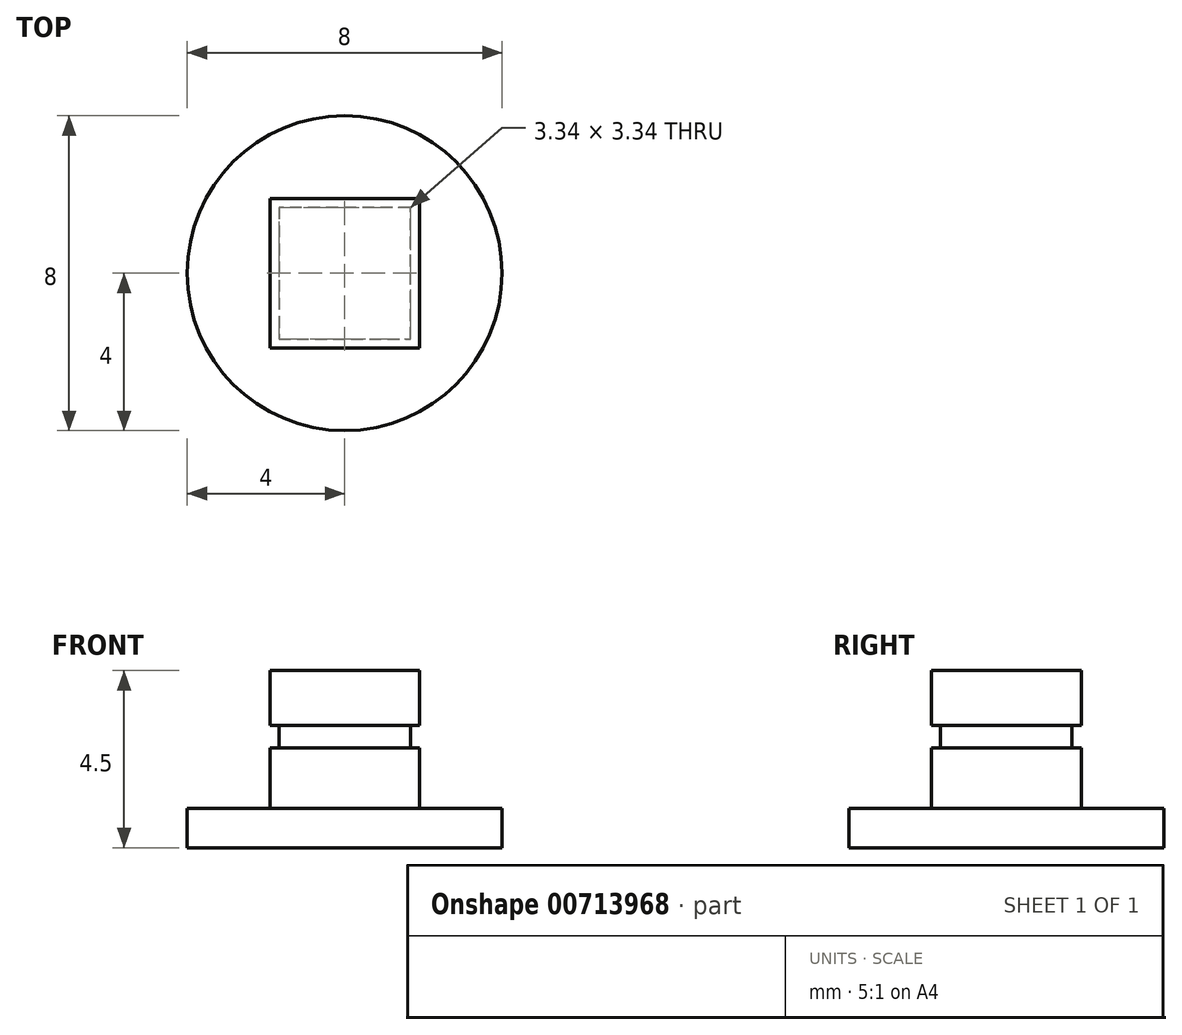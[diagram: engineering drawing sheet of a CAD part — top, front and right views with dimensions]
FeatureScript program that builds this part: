
annotation { "Feature Type Name" : "Feature", "Feature Type Description" : "" }
export const myFeature = defineFeature(function(context is Context, id is Id, definition is map)
    precondition{}
    {
        {
            var Q0;
            Q0=qCreatedBy(makeId("Top.planeOp"),FACE);
            var sketch = newSketch(context, id + "F0", { "sketchPlane" : qUnion([Q0])});
            skCircle(sketch, "E0", {"center": v(0, 0) * mm, "radius": 4 * mm});
            skSolve(sketch);
        }
        {
            var Q0;
            Q0 = qSketchRegion(id + "F0", true);
            extrude(context, id + "F1", {"entities" : qUnion([Q0]), "depth" : 1 * mm, "offsetDistance" : 25 * mm});
        }
        {
            var Q0;
            Q0=makeQuery(id+"F1.opExtrude","CAP_FACE",FACE,{"disambiguationData":[OSD([sQuery(id+"F0.wireOp",EDGE,"E0")])],"isStart":false});
            var sketch = newSketch(context, id + "F2", { "sketchPlane" : qUnion([Q0])});
            skLineSegment(sketch, "E1.bottom", {"start": v(1.9, 1.9) * mm, "end": v(-1.9, 1.9) * mm});
            skLineSegment(sketch, "E1.top", {"start": v(1.9, -1.9) * mm, "end": v(-1.9, -1.9) * mm});
            skLineSegment(sketch, "E1.left", {"start": v(1.9, 1.9) * mm, "end": v(1.9, -1.9) * mm});
            skLineSegment(sketch, "E1.right", {"start": v(-1.9, 1.9) * mm, "end": v(-1.9, -1.9) * mm});
            skPoint(sketch, "E1.middle", {"position": v(0, 0) * mm});
            skSolve(sketch);
        }
        {
            var Q0;
            Q0 = qSketchRegion(id + "F2", true);
            extrude(context, id + "F3", {"entities" : qUnion([Q0]), "operationType" : NewBodyOperationType.ADD, "depth" : 3.5 * mm, "offsetDistance" : 25 * mm});
        }
        {
            var Q0;
            Q0=qCreatedBy(makeId("Right.planeOp"),FACE);
            var sketch = newSketch(context, id + "F4", { "sketchPlane" : qUnion([Q0])});
            skLineSegment(sketch, "E2", {"start": v(0, 4.12) * mm, "end": v(0, -1.21) * mm});
            skLineSegment(sketch, "E3.bottom", {"start": v(1.9, 3.1) * mm, "end": v(1.67, 3.1) * mm});
            skLineSegment(sketch, "E3.top", {"start": v(1.9, 2.54) * mm, "end": v(1.67, 2.54) * mm});
            skLineSegment(sketch, "E3.left", {"start": v(1.9, 3.1) * mm, "end": v(1.9, 2.54) * mm});
            skLineSegment(sketch, "E3.right", {"start": v(1.67, 3.1) * mm, "end": v(1.67, 2.54) * mm});
            skSolve(sketch);
        }
        {
            var Q0;
            Q0 = qSketchRegion(id + "F4", true);
            var Q1;
            Q1=sQuery(id+"F4.wireOp",EDGE,"E3.left");
            var Q2;
            Q2=sQuery(id+"F4.wireOp",EDGE,"E3.right");
            var Q3;
            Q3=sQuery(id+"F4.wireOp",EDGE,"E3.bottom");
            var Q4;
            Q4=sQuery(id+"F4.wireOp",EDGE,"E3.top");
            extrude(context, id + "F5", {"entities" : qUnion([Q0]), "surfaceOperationType" : NewSurfaceOperationType.ADD, "surfaceEntities" : qUnion([Q1, Q2, Q3, Q4]), "endBound" : BoundingType.SYMMETRIC, "depth" : 3.8 * mm, "offsetDistance" : 25 * mm});
        }
        {
            var Q0;
            Q0=makeQuery(id+"F5.opExtrude","SWEPT_BODY",BODY,{"disambiguationData":[OSD([sQuery(id+"F4.wireOp",EDGE,"E3.bottom"),sQuery(id+"F4.wireOp",EDGE,"E3.top"),sQuery(id+"F4.wireOp",EDGE,"E3.left"),sQuery(id+"F4.wireOp",EDGE,"E3.right")])]});
            var Q1;
            Q1=sQuery(id+"F4.wireOp",EDGE,"E2");
            circularPattern(context, id + "F6", {"operationType" : NewBodyOperationType.REMOVE, "entities" : qUnion([Q0]), "axis" : qUnion([Q1]), "angle" : 360 * degree, "instanceCount" : 4, "equalSpace" : true});
        }
    });
